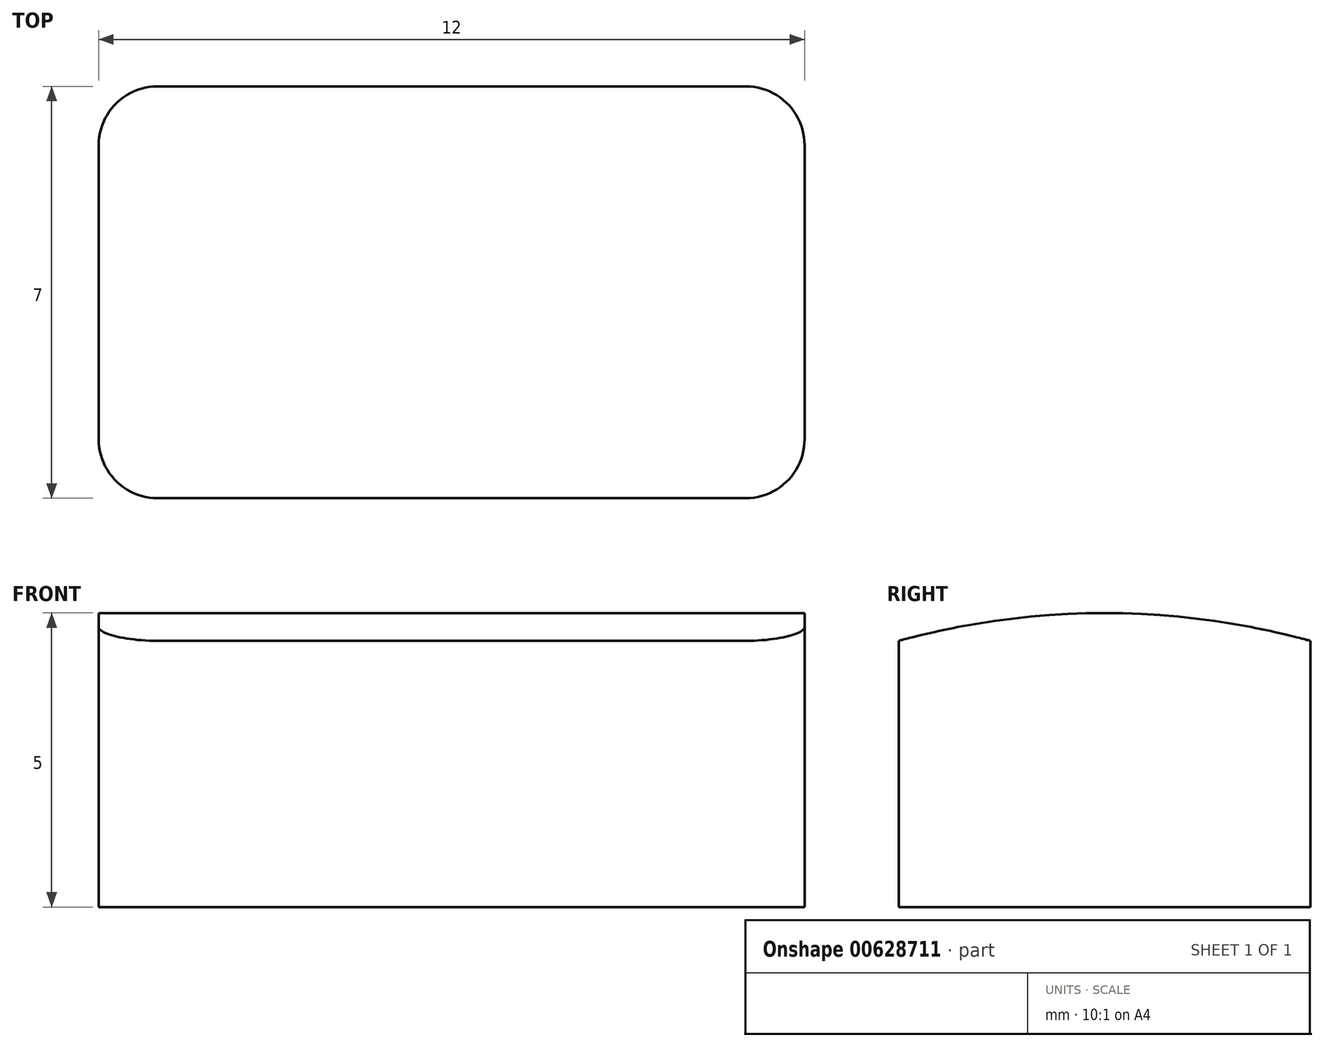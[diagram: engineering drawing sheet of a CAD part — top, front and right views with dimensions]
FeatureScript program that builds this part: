
annotation { "Feature Type Name" : "Feature", "Feature Type Description" : "" }
export const myFeature = defineFeature(function(context is Context, id is Id, definition is map)
    precondition{}
    {
        {
            var Q0;
            Q0=qCreatedBy(makeId("Right.planeOp"),FACE);
            var sketch = newSketch(context, id + "F0", { "sketchPlane" : qUnion([Q0])});
            skLineSegment(sketch, "E0.bottom", {"start": v(3.5, -2.26) * mm, "end": v(-3.5, -2.26) * mm});
            skLineSegment(sketch, "E0.top", {"start": v(3.5, 2.26) * mm, "end": v(-3.5, 2.26) * mm, "construction": true});
            skLineSegment(sketch, "E0.left", {"start": v(3.5, -2.26) * mm, "end": v(3.5, 2.26) * mm});
            skLineSegment(sketch, "E0.right", {"start": v(-3.5, -2.26) * mm, "end": v(-3.5, 2.26) * mm});
            skPoint(sketch, "E0.middle", {"position": v(0, 0) * mm});
            skArc(sketch, "E1", {"start": v(3.5, 2.26) * mm, "mid": v(0, 2.74) * mm, "end": v(-3.5, 2.26) * mm});
            skSolve(sketch);
        }
        {
            var Q0;
            Q0 = qSketchRegion(id + "F0", true);
            extrude(context, id + "F1", {"entities" : qUnion([Q0]), "endBound" : BoundingType.SYMMETRIC, "depth" : 12 * mm, "offsetDistance" : 25 * mm});
        }
        {
            var Q0;
            Q0=makeQuery(id+"F1.opExtrude","CAP_EDGE",EDGE,{"disambiguationData":[OSD([sQuery(id+"F0.wireOp",EDGE,"E0.right")])],"isStart":false});
            var Q1;
            Q1=makeQuery(id+"F1.opExtrude","CAP_EDGE",EDGE,{"disambiguationData":[OSD([sQuery(id+"F0.wireOp",EDGE,"E0.left")])],"isStart":false});
            var Q2;
            Q2=makeQuery(id+"F1.opExtrude","CAP_EDGE",EDGE,{"disambiguationData":[OSD([sQuery(id+"F0.wireOp",EDGE,"E0.left")])],"isStart":true});
            var Q3;
            Q3=makeQuery(id+"F1.opExtrude","CAP_EDGE",EDGE,{"disambiguationData":[OSD([sQuery(id+"F0.wireOp",EDGE,"E0.right")])],"isStart":true});
            fillet(context, id + "F2", {"entities" : qUnion([Q0, Q1, Q2, Q3]), "radius" : 1 * mm, "tangentPropagation" : true, "allowEdgeOverflow" : false});
        }
    });
